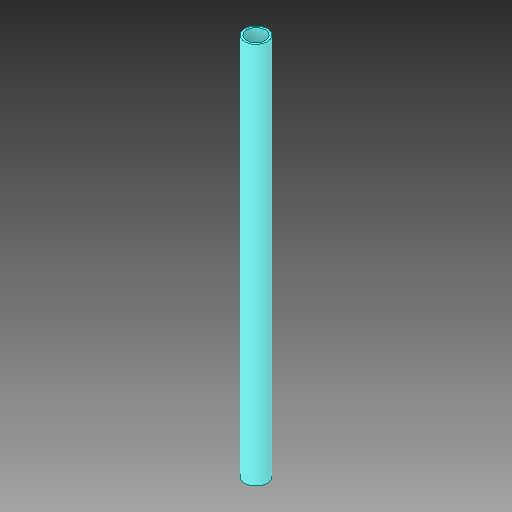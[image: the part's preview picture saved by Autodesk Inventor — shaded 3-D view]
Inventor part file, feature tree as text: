
AUTODESK INVENTOR PART (.ipt)
format: ipt  version: 2018 (Build 220112000, 112)  size: 93,696 bytes
history: native  units: in
note: dims shown in document units (in); Inventor stores cm internally (conversion verified against a paired STEP export)
features: extrude x1, sketch x1
ambient origin geometry x8: Origin, YZ Plane, XZ Plane, XY Plane, X Axis, Y Axis, Z Axis, Center Point
bodies: Solid1 (feature_tree)
feature tree (2):
  extrude  "Extrusion1"  Depth=6.329in
  sketch  "Sketch1"  dims[d0=0.375in d1=0.31in d2=6.329in d3=0.0in]
